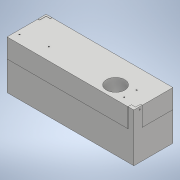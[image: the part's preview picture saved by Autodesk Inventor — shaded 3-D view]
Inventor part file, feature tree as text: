
AUTODESK INVENTOR PART (.ipt)
format: ipt  version: 2020 (Build 240168000, 168)  size: 408,576 bytes
history: native  units: mm
features: sketch x17, other x13, extrude x11, hole x5
ambient origin geometry x8: Origin, YZ Plane, XZ Plane, XY Plane, X Axis, Y Axis, Z Axis, Center Point
bodies: Body1 (feature_tree), Body2 (feature_tree)
feature tree (46):
  other  "Твердое тело1"
  extrude  "Выдавливание1"  Depth=152.5mm
  extrude  "Выдавливание2"  Depth=47.0mm
  extrude  "Выдавливание4"  Depth=30.0mm TaperAngle=0.0deg
  extrude  "Выдавливание7"  Depth=22.5mm
  extrude  "Выдавливание8"  Depth=3.0mm TaperAngle=0.0deg
  extrude  "Выдавливание9"  Depth=2.0mm
  other  "РабПлоскость1"
  other  "Разделение1"
  extrude  "Выдавливание26"  Depth=3.0mm TaperAngle=0.0deg
  extrude  "Выдавливание27"  Depth=22.0mm
  extrude  "Выдавливание28"  Depth=25.5mm
  sketch  "Эскиз25"
  hole  "Отверстие1"  [1 undecoded]
  extrude  "Выдавливание31"  Depth=2.0mm
  extrude  "Выдавливание32"  Depth=53.0mm TaperAngle=0.0deg
  hole  "Отверстие4"  [1 undecoded]
  hole  "Отверстие5"  [1 undecoded]
  hole  "Отверстие6"  [1 undecoded]
  hole  "Отверстие7"  [1 undecoded]
  sketch  "Эскиз1"
  sketch  "Эскиз2"
  sketch  "Эскиз3"
  sketch  "Эскиз4"
  sketch  "Эскиз6"
  sketch  "Эскиз7"
  sketch  "Эскиз20"
  sketch  "Эскиз22"
  sketch  "Эскиз23"
  sketch  "Эскиз24"
  sketch  "Эскиз28"
  sketch  "Эскиз29"
  sketch  "Эскиз30"
  sketch  "Эскиз31"
  sketch  "Эскиз32"
  sketch  "Эскиз33"
  other  "Проецирование ребер1"
  other  "Проецирование ребер3"
  other  "Твердое тело2"
  other  "Твердое тело3"
  other  "Проецирование ребер7"
  other  "Проецирование ребер8"
  other  "Проецирование ребер9"
  other  "Проецирование ребер10"
  other  "Проецирование ребер11"
  other  "Проецирование ребер12"
note: 5 required parameter values undecoded (feature->parameter linkage not recoverable at this tier; creation-order binding heuristic only, values carry confidence <= 0.55)
